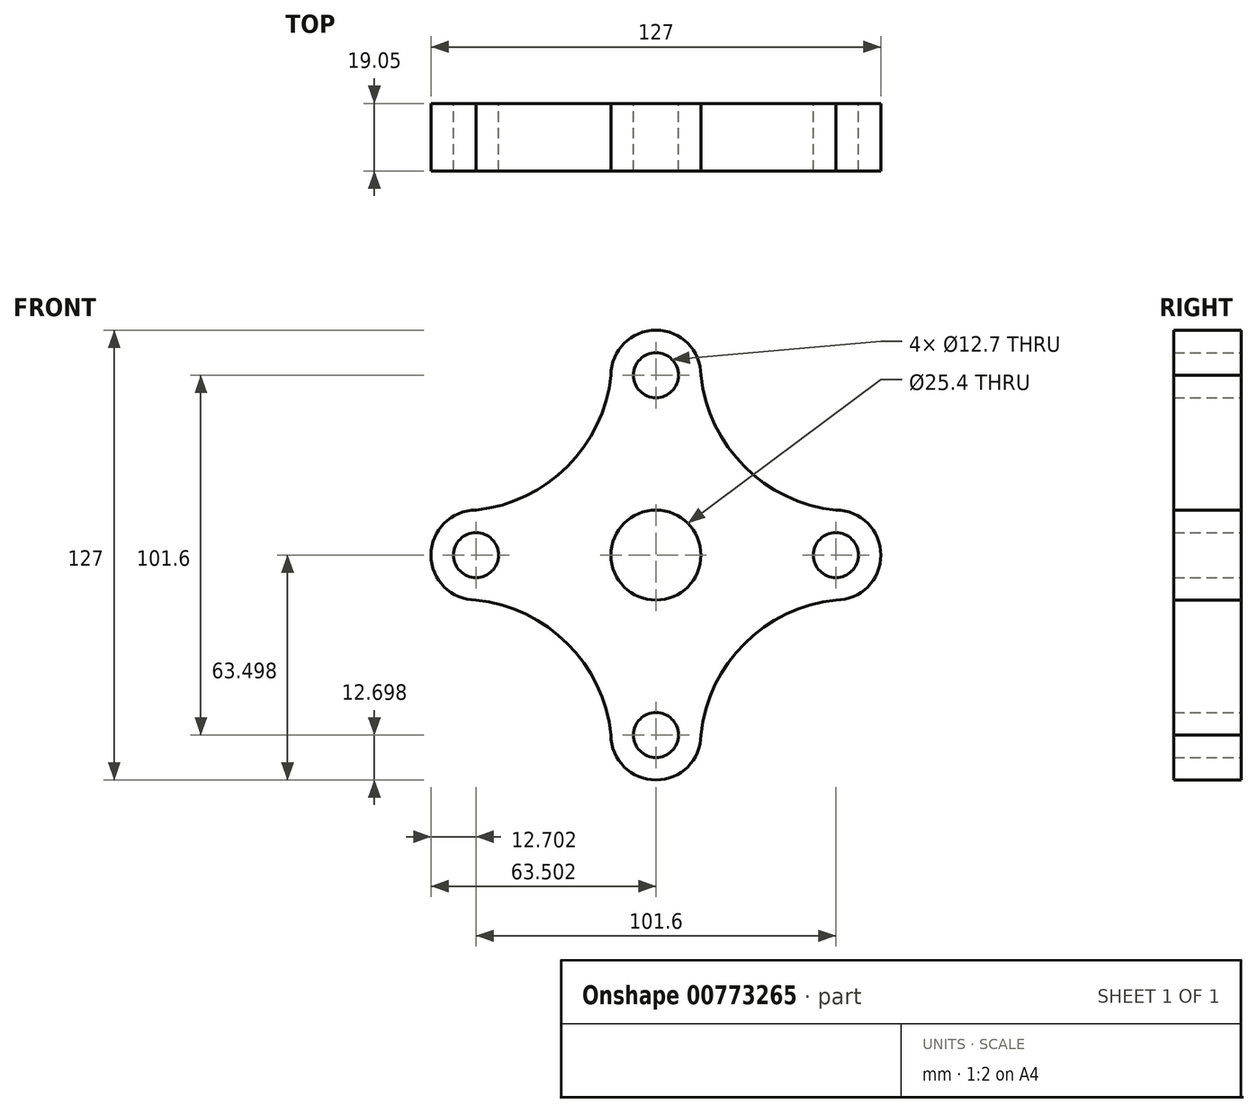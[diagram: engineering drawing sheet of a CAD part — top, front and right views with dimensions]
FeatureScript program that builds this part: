
annotation { "Feature Type Name" : "Feature", "Feature Type Description" : "" }
export const myFeature = defineFeature(function(context is Context, id is Id, definition is map)
    precondition{}
    {
        {
            var Q0;
            Q0=qCreatedBy(makeId("Front.planeOp"),FACE);
            var sketch = newSketch(context, id + "F0", { "sketchPlane" : qUnion([Q0])});
            skCircle(sketch, "E0", {"center": v(-50.8, 0) * mm, "radius": 6.35 * mm});
            skCircle(sketch, "E1", {"center": v(50.8, 0) * mm, "radius": 6.35 * mm});
            skCircle(sketch, "E2", {"center": v(0, 0) * mm, "radius": 12.7 * mm});
            skCircle(sketch, "E3", {"center": v(0, -50.8) * mm, "radius": 6.35 * mm});
            skCircle(sketch, "E4", {"center": v(0, 50.8) * mm, "radius": 6.35 * mm});
            skArc(sketch, "E5", {"start": v(-50.8, 12.7) * mm, "mid": v(-25.02, 25.02) * mm, "end": v(-12.7, 50.8) * mm});
            skArc(sketch, "E6", {"start": v(12.7, 50.8) * mm, "mid": v(0, 63.5) * mm, "end": v(-12.7, 50.8) * mm});
            skArc(sketch, "E7", {"start": v(-50.8, 12.7) * mm, "mid": v(-63.5, 0) * mm, "end": v(-50.8, -12.7) * mm});
            skPoint(sketch, "E8.trimOffspring.end.orphan", {"position": v(-50.8, 50.8) * mm});
            skArc(sketch, "E9", {"start": v(12.7, 50.8) * mm, "mid": v(24.98, 24.98) * mm, "end": v(50.8, 12.7) * mm});
            skArc(sketch, "E10", {"start": v(50.8, -12.7) * mm, "mid": v(63.5, 0) * mm, "end": v(50.8, 12.7) * mm});
            skPoint(sketch, "E11.orphan", {"position": v(50.8, 50.8) * mm});
            skArc(sketch, "E12", {"start": v(50.8, -12.7) * mm, "mid": v(24.98, -24.98) * mm, "end": v(12.7, -50.8) * mm});
            skArc(sketch, "E13", {"start": v(-12.7, -50.8) * mm, "mid": v(0, -63.5) * mm, "end": v(12.7, -50.8) * mm});
            skArc(sketch, "E14", {"start": v(-12.7, -50.8) * mm, "mid": v(-24.98, -24.98) * mm, "end": v(-50.8, -12.7) * mm});
            skPoint(sketch, "E15.orphan", {"position": v(-50.8, -50.8) * mm});
            skPoint(sketch, "E16.orphan", {"position": v(50.8, -50.8) * mm});
            skSolve(sketch);
        }
        {
            var Q0;
            Q0 = qSketchRegion(id + "F0", true);
            extrude(context, id + "F1", {"entities" : qUnion([Q0]), "depth" : 19.05 * mm, "offsetDistance" : 25.4 * mm});
        }
    });
